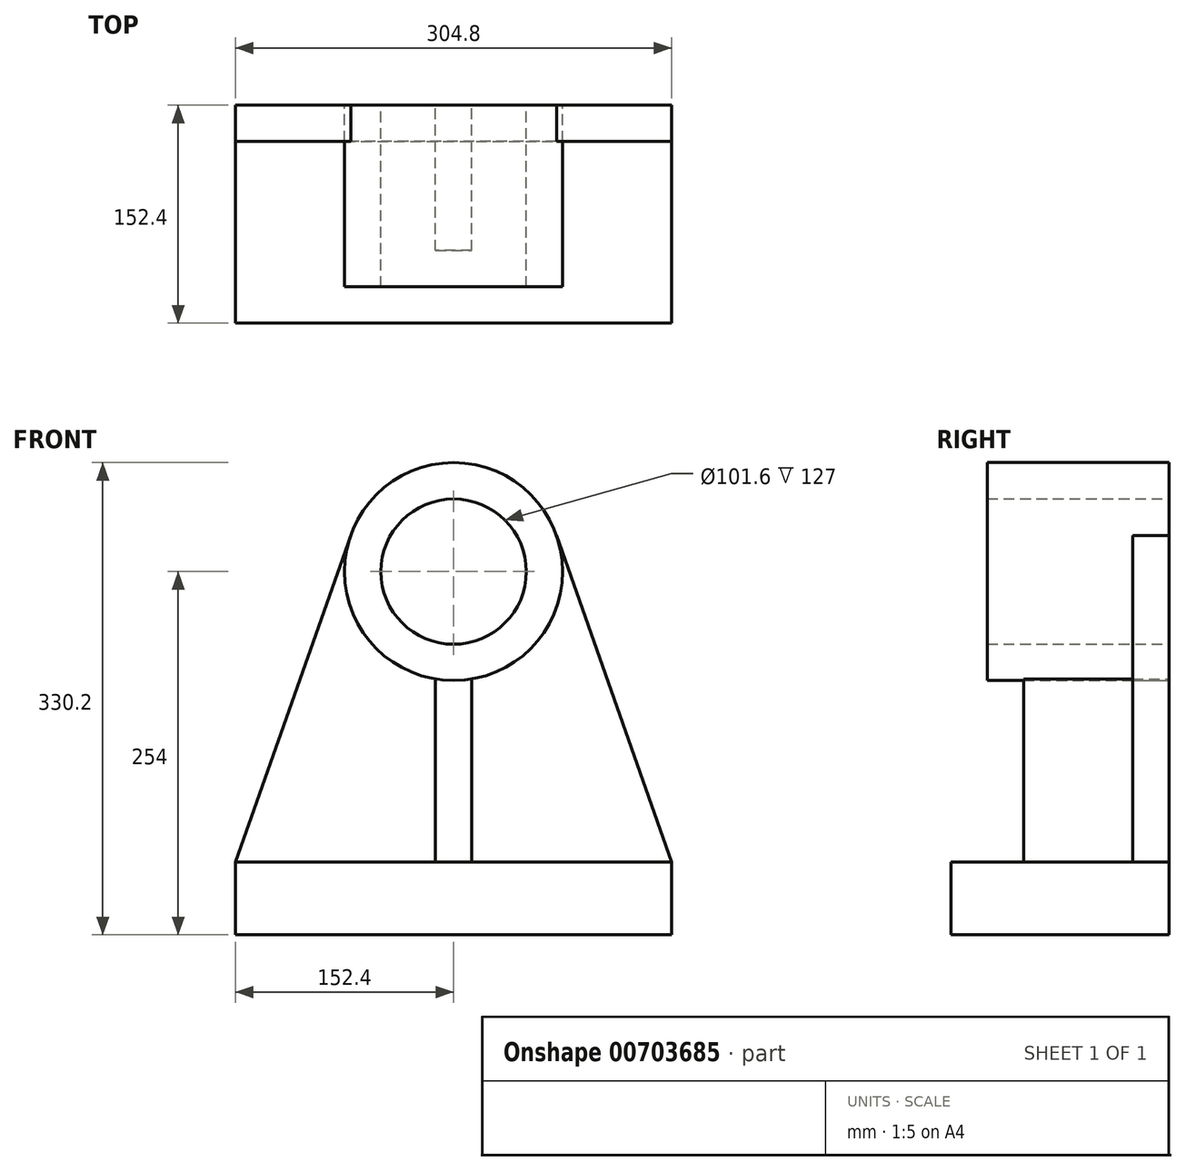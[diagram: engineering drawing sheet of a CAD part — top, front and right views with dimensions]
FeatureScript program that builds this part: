
annotation { "Feature Type Name" : "Feature", "Feature Type Description" : "" }
export const myFeature = defineFeature(function(context is Context, id is Id, definition is map)
    precondition{}
    {
        {
            var Q0;
            Q0=qCreatedBy(makeId("Front.planeOp"),FACE);
            var sketch = newSketch(context, id + "F0", { "sketchPlane" : qUnion([Q0])});
            skLineSegment(sketch, "E0.bottom", {"start": v(152.4, -25.4) * mm, "end": v(-152.4, -25.4) * mm});
            skLineSegment(sketch, "E0.top", {"start": v(152.4, 25.4) * mm, "end": v(-152.4, 25.4) * mm});
            skLineSegment(sketch, "E0.left", {"start": v(152.4, -25.4) * mm, "end": v(152.4, 25.4) * mm});
            skLineSegment(sketch, "E0.right", {"start": v(-152.4, -25.4) * mm, "end": v(-152.4, 25.4) * mm});
            skPoint(sketch, "E0.middle", {"position": v(0, 0) * mm});
            skCircle(sketch, "E1", {"center": v(0, 228.6) * mm, "radius": 76.2 * mm});
            skCircle(sketch, "E2", {"center": v(0, 228.6) * mm, "radius": 50.8 * mm});
            skLineSegment(sketch, "E3", {"start": v(152.4, 25.4) * mm, "end": v(77.46, 238.05) * mm});
            skLineSegment(sketch, "E4", {"start": v(-152.4, 25.4) * mm, "end": v(-80.72, 228.8) * mm});
            skLineSegment(sketch, "E5", {"start": v(-12.7, 25.4) * mm, "end": v(-12.7, 153.47) * mm});
            skLineSegment(sketch, "E6", {"start": v(12.7, 25.4) * mm, "end": v(12.7, 153.47) * mm});
            skSolve(sketch);
        }
        {
            var Q0;
            Q0=makeQuery(id+"F0.imprint","IMPRINT",FACE,{"disambiguationData":[TD([[makeQuery(id+"F0.imprint","IMPRINT",EDGE,{"derivedFrom":sQuery(id+"F0.wireOp",EDGE,"E0.bottom")}),-1.0]])]});
            extrude(context, id + "F1", {"entities" : qUnion([Q0]), "depth" : 152.4 * mm, "offsetDistance" : 25.4 * mm});
        }
        {
            var Q0;
            Q0=qCreatedBy(makeId("Front.planeOp"),FACE);
            var sketch = newSketch(context, id + "F2", { "sketchPlane" : qUnion([Q0])});
            skCircle(sketch, "E7", {"center": v(0, 228.6) * mm, "radius": 76.2 * mm});
            skCircle(sketch, "E8", {"center": v(0, 228.6) * mm, "radius": 50.8 * mm});
            skSolve(sketch);
        }
        {
            var Q0;
            Q0 = qSketchRegion(id + "F2", true);
            extrude(context, id + "F3", {"entities" : qUnion([Q0]), "depth" : 127 * mm, "offsetDistance" : 25.4 * mm});
        }
        {
            var Q0;
            Q0=qCreatedBy(makeId("Front.planeOp"),FACE);
            var sketch = newSketch(context, id + "F4", { "sketchPlane" : qUnion([Q0])});
            skLineSegment(sketch, "E9", {"start": v(-12.7, 25.4) * mm, "end": v(-12.7, 153.47) * mm});
            skLineSegment(sketch, "E10", {"start": v(12.7, 25.4) * mm, "end": v(12.7, 153.47) * mm});
            skCircle(sketch, "E11.0", {"center": v(0, 228.6) * mm, "radius": 76.2 * mm});
            skLineSegment(sketch, "E12.0", {"start": v(152.4, 25.4) * mm, "end": v(-152.4, 25.4) * mm});
            skSolve(sketch);
        }
        {
            var Q0;
            {var subQ0=sQuery(id+"F4.wireOp",EDGE,"E9");Q0=makeQuery(id+"F4.imprint","IMPRINT",FACE,{"disambiguationData":[TD([[makeQuery(id+"F4.imprint","IMPRINT",EDGE,{"derivedFrom":subQ0}),-1.0]])]});}
            extrude(context, id + "F5", {"entities" : qUnion([Q0]), "depth" : 101.6 * mm, "offsetDistance" : 25.4 * mm});
        }
        {
            var Q0;
            Q0=qCreatedBy(makeId("Front.planeOp"),FACE);
            var sketch = newSketch(context, id + "F6", { "sketchPlane" : qUnion([Q0])});
            skCircle(sketch, "E13.0", {"center": v(0, 228.6) * mm, "radius": 76.2 * mm});
            skLineSegment(sketch, "E14.0", {"start": v(152.4, -25.4) * mm, "end": v(152.4, 25.4) * mm});
            skLineSegment(sketch, "E14.1", {"start": v(-152.4, -25.4) * mm, "end": v(152.4, -25.4) * mm});
            skLineSegment(sketch, "E14.2", {"start": v(-152.4, 25.4) * mm, "end": v(-152.4, -25.4) * mm});
            skLineSegment(sketch, "E14.3", {"start": v(152.4, 25.4) * mm, "end": v(-152.4, 25.4) * mm});
            skLineSegment(sketch, "E15", {"start": v(152.4, 25.4) * mm, "end": v(71.87, 253.93) * mm});
            skLineSegment(sketch, "E16", {"start": v(-152.4, 25.4) * mm, "end": v(-71.87, 253.93) * mm});
            skSolve(sketch);
        }
        {
            var Q0;
            Q0=makeQuery(id+"F6.imprint","IMPRINT",FACE,{"disambiguationData":[TD([[makeQuery(id+"F6.imprint","IMPRINT",EDGE,{"derivedFrom":sQuery(id+"F6.wireOp",EDGE,"E14.3")}),-1.0]])]});
            extrude(context, id + "F7", {"entities" : qUnion([Q0]), "depth" : 25.4 * mm, "offsetDistance" : 25.4 * mm});
        }
    });
